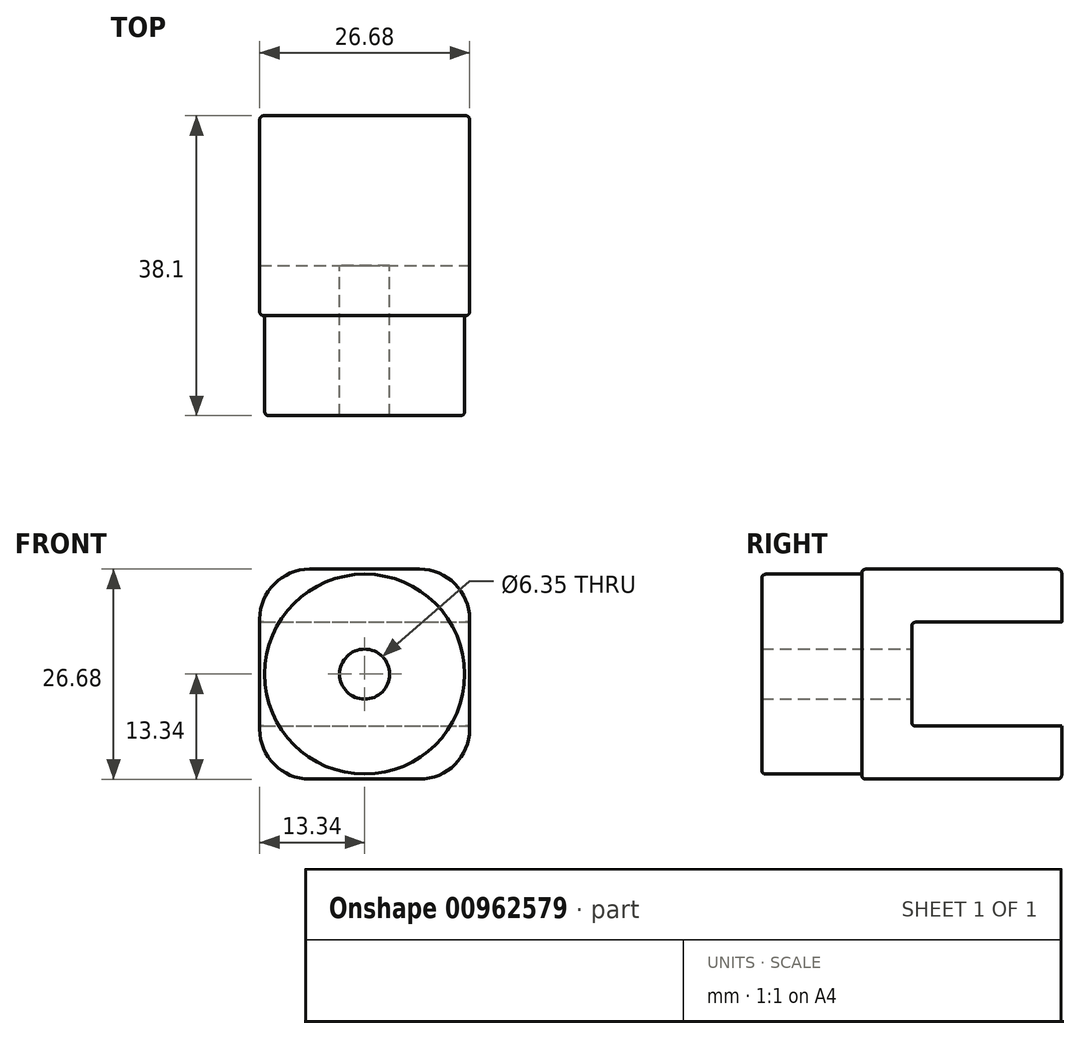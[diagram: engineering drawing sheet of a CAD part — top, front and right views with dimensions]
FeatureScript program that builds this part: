
annotation { "Feature Type Name" : "Feature", "Feature Type Description" : "" }
export const myFeature = defineFeature(function(context is Context, id is Id, definition is map)
    precondition{}
    {
        {
            var Q0;
            Q0=qCreatedBy(makeId("Front.planeOp"),FACE);
            var sketch = newSketch(context, id + "F0", { "sketchPlane" : qUnion([Q0])});
            skCircle(sketch, "E0", {"center": v(0, 0) * mm, "radius": 12.7 * mm});
            skCircle(sketch, "E1", {"center": v(0, 0) * mm, "radius": 3.18 * mm});
            skSolve(sketch);
        }
        {
            var Q0;
            Q0 = qSketchRegion(id + "F0", true);
            extrude(context, id + "F1", {"entities" : qUnion([Q0]), "endBound" : BoundingType.SYMMETRIC, "depth" : 25.4 * mm, "offsetDistance" : 25.4 * mm});
        }
        {
            var Q0;
            Q0=qCreatedBy(makeId("Front.planeOp"),FACE);
            var sketch = newSketch(context, id + "F2", { "sketchPlane" : qUnion([Q0])});
            skLineSegment(sketch, "E2.bottom", {"start": v(-13.33, -13.34) * mm, "end": v(13.34, -13.34) * mm});
            skLineSegment(sketch, "E2.top", {"start": v(-13.34, 13.34) * mm, "end": v(13.33, 13.34) * mm});
            skLineSegment(sketch, "E2.left", {"start": v(-13.34, -13.34) * mm, "end": v(-13.34, 13.34) * mm});
            skLineSegment(sketch, "E2.right", {"start": v(13.34, -13.34) * mm, "end": v(13.33, 13.34) * mm});
            skPoint(sketch, "E2.middle", {"position": v(0, 0) * mm});
            skCircle(sketch, "E3", {"center": v(0, 0) * mm, "radius": 6.35 * mm});
            skSolve(sketch);
        }
        {
            var Q0;
            Q0 = qSketchRegion(id + "F2", true);
            extrude(context, id + "F3", {"entities" : qUnion([Q0]), "operationType" : NewBodyOperationType.ADD, "oppositeDirection" : true, "depth" : 25.4 * mm, "offsetDistance" : 25.4 * mm});
        }
        {
            var Q0;
            Q0=makeQuery(id+"F3.opExtrude","CAP_FACE",FACE,{"disambiguationData":[OSD([sQuery(id+"F2.wireOp",EDGE,"E2.bottom"),sQuery(id+"F2.wireOp",EDGE,"E2.top"),sQuery(id+"F2.wireOp",EDGE,"E2.left"),sQuery(id+"F2.wireOp",EDGE,"E2.right")])],"isStart":false});
            var sketch = newSketch(context, id + "F4", { "sketchPlane" : qUnion([Q0])});
            skLineSegment(sketch, "E4.bottom", {"start": v(13.34, -6.6) * mm, "end": v(-13.34, -6.6) * mm});
            skLineSegment(sketch, "E4.top", {"start": v(13.34, 6.6) * mm, "end": v(-13.34, 6.6) * mm});
            skLineSegment(sketch, "E4.left", {"start": v(13.34, -6.6) * mm, "end": v(13.34, 6.6) * mm});
            skLineSegment(sketch, "E4.right", {"start": v(-13.34, -6.6) * mm, "end": v(-13.34, 6.6) * mm});
            skPoint(sketch, "E4.middle", {"position": v(0, 0) * mm});
            skSolve(sketch);
        }
        {
            var Q0;
            Q0 = qSketchRegion(id + "F4", true);
            extrude(context, id + "F5", {"entities" : qUnion([Q0]), "operationType" : NewBodyOperationType.REMOVE, "oppositeDirection" : true, "depth" : 19.05 * mm, "offsetDistance" : 25.4 * mm});
        }
        {
            var Q0;
            Q0=makeQuery(id+"F1.opExtrude","CAP_EDGE",EDGE,{"disambiguationData":[OSD([sQuery(id+"F0.wireOp",EDGE,"E0")])],"isStart":false});
            fillet(context, id + "F6", {"entities" : qUnion([Q0]), "radius" : 0.5 * mm, "tangentPropagation" : true, "allowEdgeOverflow" : false});
        }
        {
            var Q0;
            Q0=makeQuery(id+"F3.opExtrude","SWEPT_EDGE",EDGE,{"disambiguationData":[OSD([sQuery(id+"F2.wireOp",EDGE,"E2.top"),sQuery(id+"F2.wireOp",EDGE,"E2.right")])]});
            var Q1;
            Q1=makeQuery(id+"F3.opExtrude","SWEPT_EDGE",EDGE,{"disambiguationData":[OSD([sQuery(id+"F2.wireOp",EDGE,"E2.top"),sQuery(id+"F2.wireOp",EDGE,"E2.left")])]});
            var Q2;
            Q2=makeQuery(id+"F3.opExtrude","SWEPT_EDGE",EDGE,{"disambiguationData":[OSD([sQuery(id+"F2.wireOp",EDGE,"E2.bottom"),sQuery(id+"F2.wireOp",EDGE,"E2.left")])]});
            var Q3;
            Q3=makeQuery(id+"F3.opExtrude","SWEPT_EDGE",EDGE,{"disambiguationData":[OSD([sQuery(id+"F2.wireOp",EDGE,"E2.bottom"),sQuery(id+"F2.wireOp",EDGE,"E2.right")])]});
            fillet(context, id + "F7", {"entities" : qUnion([Q0, Q1, Q2, Q3]), "radius" : 6.35 * mm, "tangentPropagation" : true, "allowEdgeOverflow" : false});
        }
        {
            var Q0;
            {var subQ0=sQuery(id+"F2.wireOp",EDGE,"E2.right");var subQ1=sQuery(id+"F2.wireOp",EDGE,"E2.top");Q0=makeQuery(id+"F7.opFillet","BLEND_EDGE",EDGE,{"blendedFrom":[makeQuery(id+"F3.opExtrude","SWEPT_EDGE",EDGE,{"disambiguationData":[OSD([subQ1,subQ0])]}),makeQuery(id+"F3.opExtrude","CAP_FACE",FACE,{"disambiguationData":[OSD([sQuery(id+"F2.wireOp",EDGE,"E2.bottom"),subQ1,sQuery(id+"F2.wireOp",EDGE,"E2.left"),subQ0])],"isStart":true})],"blendedInto":[makeQuery(id+"F3.opExtrude","CAP_FACE",FACE,{"disambiguationData":[OSD([sQuery(id+"F2.wireOp",EDGE,"E2.bottom"),subQ1,sQuery(id+"F2.wireOp",EDGE,"E2.left"),subQ0])],"isStart":true})]});}
            fillet(context, id + "F8", {"entities" : qUnion([Q0]), "radius" : 0.5 * mm, "tangentPropagation" : true, "allowEdgeOverflow" : false});
        }
        {
            var Q0;
            Q0=makeQuery(id+"F3.opExtrude","CAP_EDGE",EDGE,{"disambiguationData":[OSD([sQuery(id+"F2.wireOp",EDGE,"E2.top")])],"isStart":false});
            var Q1;
            Q1=makeQuery(id+"F3.opExtrude","CAP_EDGE",EDGE,{"disambiguationData":[OSD([sQuery(id+"F2.wireOp",EDGE,"E2.bottom")])],"isStart":false});
            var Q2;
            Q2=makeQuery(id+"F5.boolean.opBoolean","COPY",EDGE,{"derivedFrom":makeQuery(id+"F5.opExtrude","CAP_EDGE",EDGE,{"disambiguationData":[OSD([sQuery(id+"F4.wireOp",EDGE,"E4.top")])],"isStart":false})});
            var Q3;
            Q3=makeQuery(id+"F5.boolean.opBoolean","COPY",EDGE,{"derivedFrom":makeQuery(id+"F5.opExtrude","CAP_EDGE",EDGE,{"disambiguationData":[OSD([sQuery(id+"F4.wireOp",EDGE,"E4.bottom")])],"isStart":false})});
            fillet(context, id + "F9", {"entities" : qUnion([Q0, Q1, Q2, Q3]), "radius" : 0.5 * mm, "tangentPropagation" : true, "allowEdgeOverflow" : false});
        }
    });
